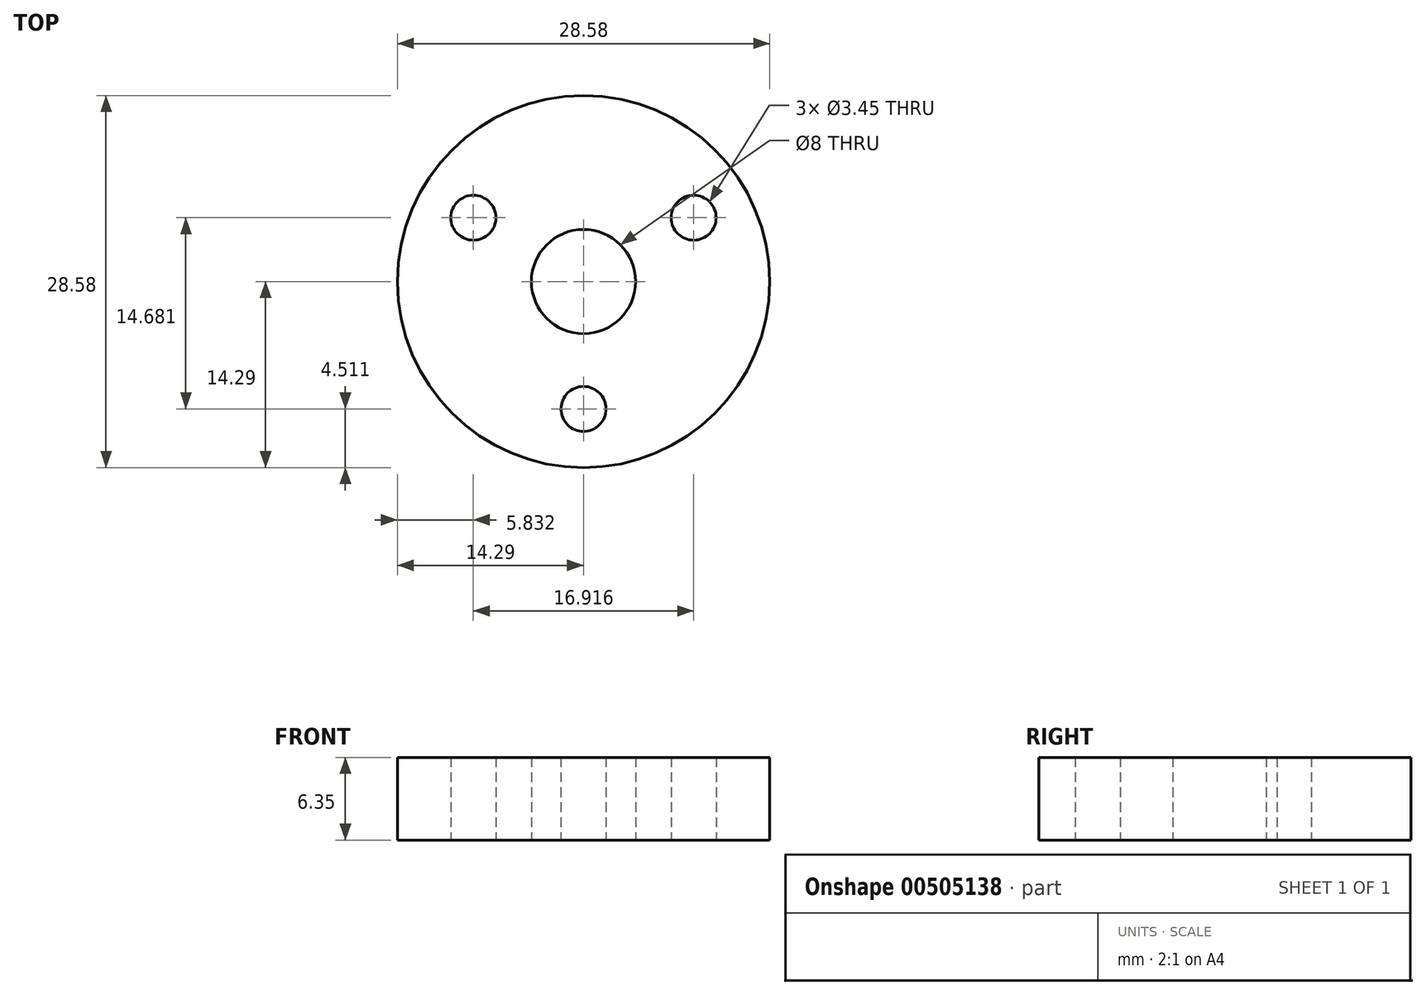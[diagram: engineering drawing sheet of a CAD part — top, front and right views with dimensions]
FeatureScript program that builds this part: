
annotation { "Feature Type Name" : "Feature", "Feature Type Description" : "" }
export const myFeature = defineFeature(function(context is Context, id is Id, definition is map)
    precondition{}
    {
        {
            var Q0;
            Q0=qCreatedBy(makeId("Top.planeOp"),FACE);
            var sketch = newSketch(context, id + "F0", { "sketchPlane" : qUnion([Q0])});
            skCircle(sketch, "E0", {"center": v(0, 0) * mm, "radius": 14.29 * mm});
            skCircle(sketch, "E1", {"center": v(0, 0) * mm, "radius": 4 * mm});
            skCircle(sketch, "E2", {"center": v(0, -9.78) * mm, "radius": 1.73 * mm});
            skCircle(sketch, "E3", {"center": v(8.46, 4.9) * mm, "radius": 1.73 * mm});
            skCircle(sketch, "E4", {"center": v(-8.46, 4.9) * mm, "radius": 1.73 * mm});
            skLineSegment(sketch, "E5", {"start": v(-14.29, 0) * mm, "end": v(14.29, 0) * mm, "construction": true});
            skLineSegment(sketch, "E6", {"start": v(0, 0) * mm, "end": v(0, 14.29) * mm, "construction": true});
            skSolve(sketch);
        }
        {
            var Q0;
            Q0=makeQuery(id+"F0.imprint","IMPRINT",FACE,{"disambiguationData":[TD([[makeQuery(id+"F0.imprint","IMPRINT",EDGE,{"derivedFrom":sQuery(id+"F0.wireOp",EDGE,"E0")}),1.0]])]});
            extrude(context, id + "F1", {"entities" : qUnion([Q0]), "depth" : 6.35 * mm});
        }
    });
